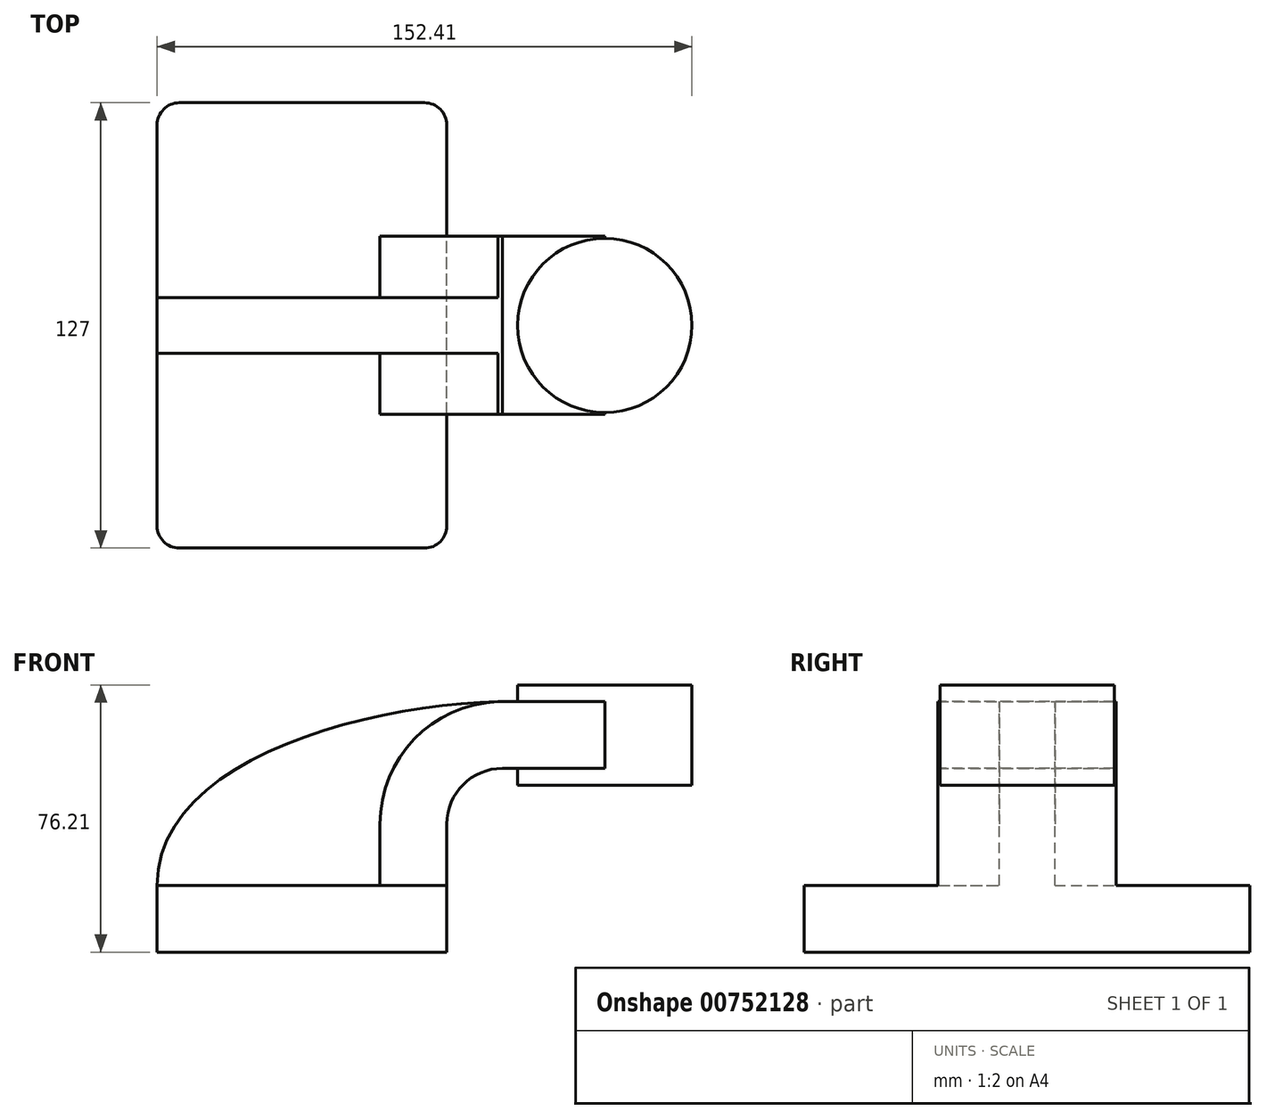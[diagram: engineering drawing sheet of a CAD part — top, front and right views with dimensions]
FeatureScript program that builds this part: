
annotation { "Feature Type Name" : "Feature", "Feature Type Description" : "" }
export const myFeature = defineFeature(function(context is Context, id is Id, definition is map)
    precondition{}
    {
        {
            var Q0;
            Q0=qCreatedBy(makeId("Front.planeOp"),FACE);
            var sketch = newSketch(context, id + "F0", { "sketchPlane" : qUnion([Q0])});
            skLineSegment(sketch, "E0.bottom", {"start": v(-41.28, 9.52) * mm, "end": v(41.27, 9.53) * mm});
            skLineSegment(sketch, "E0.top", {"start": v(-41.28, -9.52) * mm, "end": v(41.28, -9.52) * mm});
            skLineSegment(sketch, "E0.left", {"start": v(-41.28, 9.52) * mm, "end": v(-41.28, -9.53) * mm});
            skLineSegment(sketch, "E0.right", {"start": v(41.27, 9.53) * mm, "end": v(41.28, -9.52) * mm});
            skPoint(sketch, "E0.middle", {"position": v(0, 0) * mm});
            skLineSegment(sketch, "E1.bottom", {"start": v(111.12, 38.1) * mm, "end": v(60.32, 38.1) * mm});
            skLineSegment(sketch, "E1.top", {"start": v(111.12, 66.68) * mm, "end": v(60.32, 66.68) * mm});
            skLineSegment(sketch, "E1.left", {"start": v(111.12, 38.1) * mm, "end": v(111.12, 66.68) * mm});
            skLineSegment(sketch, "E1.right", {"start": v(60.32, 38.1) * mm, "end": v(60.32, 66.67) * mm});
            skPoint(sketch, "E1.middle", {"position": v(85.72, 52.39) * mm});
            skLineSegment(sketch, "E2", {"start": v(41.27, 9.53) * mm, "end": v(41.27, 27) * mm});
            skArc(sketch, "E3", {"start": v(41.27, 27) * mm, "mid": v(45.92, 38.23) * mm, "end": v(57.15, 42.88) * mm});
            skLineSegment(sketch, "E4", {"start": v(57.15, 42.88) * mm, "end": v(86.29, 42.88) * mm});
            skLineSegment(sketch, "E5.0", {"start": v(57.15, 61.93) * mm, "end": v(86.29, 61.93) * mm});
            skArc(sketch, "E5.1", {"start": v(22.22, 27) * mm, "mid": v(32.45, 51.7) * mm, "end": v(57.15, 61.93) * mm});
            skLineSegment(sketch, "E5.2", {"start": v(22.22, 9.53) * mm, "end": v(22.22, 27) * mm});
            skLineSegment(sketch, "E6", {"start": v(86.29, 42.88) * mm, "end": v(86.29, 61.93) * mm});
            skLineSegment(sketch, "E7", {"start": v(86.29, 42.88) * mm, "end": v(86.29, 38.1) * mm});
            skLineSegment(sketch, "E8", {"start": v(86.29, 38.1) * mm, "end": v(86.29, 61.93) * mm});
            skLineSegment(sketch, "E9", {"start": v(86.29, 66.68) * mm, "end": v(86.29, 61.93) * mm});
            skFitSpline(sketch, "E10", {"points": [v(-41.28, 9.53) * mm, v(57.15, 61.93) * mm], "startDerivative": vector(-0.33, 107.5) * mm, "endDerivative": vector(115.12, 1.65) * mm});
            skSolve(sketch);
        }
        {
            var Q0;
            Q0=makeQuery(id+"F0.imprint","IMPRINT",FACE,{"disambiguationData":[TD([[makeQuery(id+"F0.imprint","IMPRINT",EDGE,{"derivedFrom":sQuery(id+"F0.wireOp",EDGE,"E0.top")}),1.0]])]});
            extrude(context, id + "F1", {"entities" : qUnion([Q0]), "endBound" : BoundingType.SYMMETRIC, "depth" : 127 * mm, "offsetDistance" : 25.4 * mm});
        }
        {
            var Q0;
            {var subQ1=sQuery(id+"F0.wireOp",EDGE,"E2");Q0=makeQuery(id+"F0.imprint","IMPRINT",FACE,{"disambiguationData":[TD([[makeQuery(id+"F0.imprint","IMPRINT",EDGE,{"derivedFrom":subQ1}),1.0]])]});}
            extrude(context, id + "F2", {"entities" : qUnion([Q0]), "operationType" : NewBodyOperationType.ADD, "endBound" : BoundingType.SYMMETRIC, "depth" : 50.8 * mm, "offsetDistance" : 25.4 * mm});
        }
        {
            var Q0;
            {var subQ3=sQuery(id+"F0.wireOp",EDGE,"E5.2");Q0=makeQuery(id+"F0.imprint","IMPRINT",FACE,{"disambiguationData":[TD([[makeQuery(id+"F0.imprint","IMPRINT",EDGE,{"derivedFrom":subQ3}),1.0]])]});}
            extrude(context, id + "F3", {"entities" : qUnion([Q0]), "operationType" : NewBodyOperationType.ADD, "endBound" : BoundingType.SYMMETRIC, "depth" : 15.88 * mm, "offsetDistance" : 25.4 * mm});
        }
        {
            var Q0;
            {var subQ0=sQuery(id+"F0.wireOp",EDGE,"E4");var subQ1=sQuery(id+"F0.wireOp",EDGE,"E1.right");var subQ2=makeQuery(id+"F0.imprint","INTERSECT",VERTEX,{"derivedFrom":[subQ1,subQ0]});Q0=makeQuery(id+"F0.imprint","IMPRINT",FACE,{"disambiguationData":[TD([[makeQuery(id+"F0.imprint","IMPRINT",EDGE,{"disambiguationData":[TD([[subQ2,-1.0]])],"derivedFrom":subQ1}),-1.0]])]});}
            extrude(context, id + "F4", {"entities" : qUnion([Q0]), "operationType" : NewBodyOperationType.ADD, "endBound" : BoundingType.SYMMETRIC, "depth" : 50.8 * mm, "offsetDistance" : 25.4 * mm});
        }
        {
            var Q0;
            {var subQ0=sQuery(id+"F0.wireOp",EDGE,"E1.left");Q0=makeQuery(id+"F0.imprint","IMPRINT",FACE,{"disambiguationData":[TD([[makeQuery(id+"F0.imprint","IMPRINT",EDGE,{"derivedFrom":subQ0}),1.0]])]});}
            var Q1;
            Q1=sQuery(id+"F0.wireOp",EDGE,"E8");
            revolve(context, id + "F5", {"operationType" : NewBodyOperationType.ADD, "surfaceOperationType" : NewSurfaceOperationType.NEW, "entities" : qUnion([Q0]), "axis" : qUnion([Q1]), "revolveType" : RevolveType.FULL});
        }
        {
            var Q0;
            Q0=makeQuery(id+"F1.opExtrude","CAP_EDGE",EDGE,{"disambiguationData":[OSD([sQuery(id+"F0.wireOp",EDGE,"E0.right")])],"isStart":true});
            var Q1;
            Q1=makeQuery(id+"F1.opExtrude","CAP_EDGE",EDGE,{"disambiguationData":[OSD([sQuery(id+"F0.wireOp",EDGE,"E0.left")])],"isStart":true});
            var Q2;
            Q2=makeQuery(id+"F1.opExtrude","CAP_EDGE",EDGE,{"disambiguationData":[OSD([sQuery(id+"F0.wireOp",EDGE,"E0.left")])],"isStart":false});
            var Q3;
            Q3=makeQuery(id+"F1.opExtrude","CAP_EDGE",EDGE,{"disambiguationData":[OSD([sQuery(id+"F0.wireOp",EDGE,"E0.right")])],"isStart":false});
            fillet(context, id + "F6", {"entities" : qUnion([Q0, Q1, Q2, Q3]), "radius" : 6.35 * mm, "tangentPropagation" : true, "allowEdgeOverflow" : false});
        }
    });
